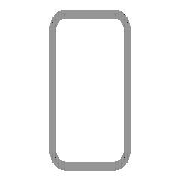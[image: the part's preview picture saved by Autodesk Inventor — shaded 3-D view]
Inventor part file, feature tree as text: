
AUTODESK INVENTOR PART (.ipt)
format: ipt  version: 2025.3 (Build 293356030, 356C)  size: 149,504 bytes
history: native  units: mm (DEFAULTED — no unit token found)
features: other x4, plane x3, split x2, sketch x1
ambient origin geometry x8: Origin, YZ Plane, XZ Plane, XY Plane, X Axis, Y Axis, Z Axis, Center Point
bodies: Solid1 (feature_tree), Body (feature_tree)
feature tree (10):
  parser-record x1  (decoder bookkeeping rows leaked as tree rows — omitted from the tree; the rows remain in map.json)
  other  "Driven Length"
  other  "Start Plane"
  other  "End Plane"
  plane  "Work Plane4"
  split  "Split1"
  plane  "Work Plane5"
  split  "Split2"
  sketch  "Sketch3"  dims[d3=359.411255mm d4=0.0mm d7=4.0mm d9=20.0mm d11=40.0mm d12=2.0mm d13=28.284271mm d14=387.695526mm d15=10.0mm d16=20.0mm d17=90.0deg d18=359.411255mm]
  plane  "Work Plane3"
